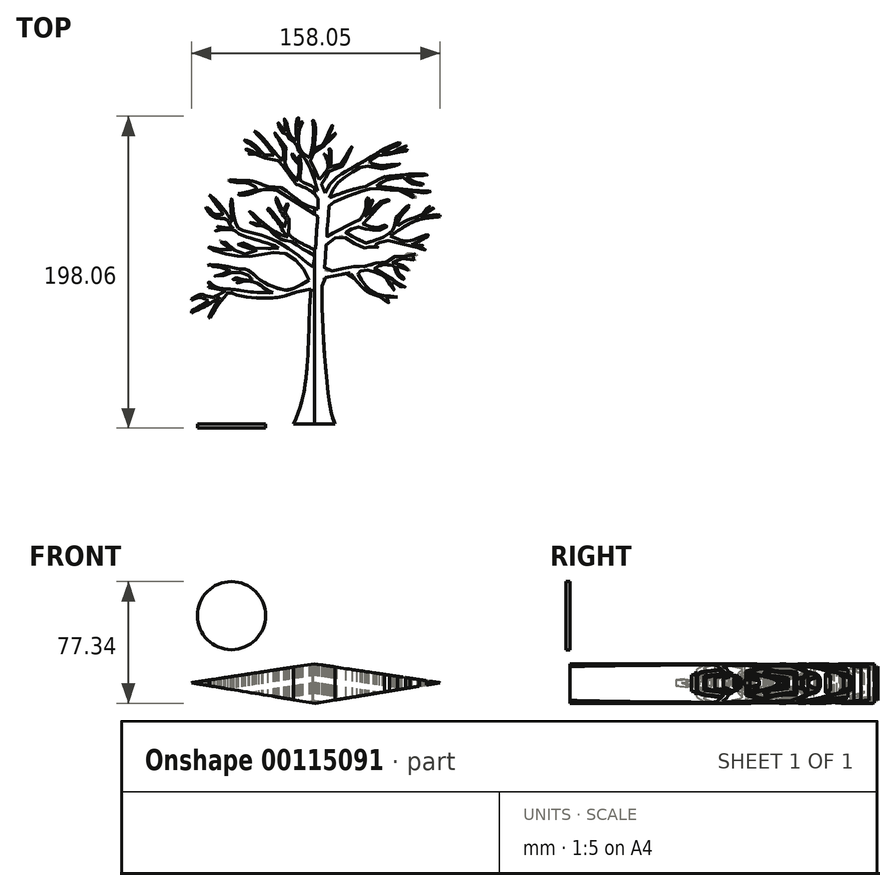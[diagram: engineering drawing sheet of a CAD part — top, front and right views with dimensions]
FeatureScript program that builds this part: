
annotation { "Feature Type Name" : "Feature", "Feature Type Description" : "" }
export const myFeature = defineFeature(function(context is Context, id is Id, definition is map)
    precondition{}
    {
        {
            var Q0;
            Q0=qCreatedBy(makeId("Top.planeOp"),FACE);
            var sketch = newSketch(context, id + "F0", { "sketchPlane" : qUnion([Q0])});
            skFitSpline(sketch, "E0", {"points": [v(-17.14, -117.95) * mm, v(-11.28, -101.28) * mm, v(-6.86, -42.52) * mm, v(-6.02, -32.17) * mm], "startDerivative": vector(3.93, 13.73) * mm, "endDerivative": vector(1.9, 26.28) * mm});
            skFitSpline(sketch, "E1", {"points": [v(-6.02, -32.17) * mm, v(-14.74, -34.04) * mm, v(-27.66, -37.49) * mm, v(-54.51, -35.53) * mm, v(-58.1, -34.04) * mm, v(-60.6, -36.76) * mm, v(-65.35, -42.8) * mm, v(-70.21, -50.73) * mm], "startDerivative": vector(-61.25, -20.1) * mm, "endDerivative": vector(-32.79, -56.2) * mm});
            skFitSpline(sketch, "E2", {"points": [v(-70.21, -50.73) * mm, v(-70.69, -50.15) * mm, v(-63.82, -37.26) * mm], "startDerivative": vector(-3.59, 1.97) * mm, "endDerivative": vector(12.9, 20.96) * mm});
            skFitSpline(sketch, "E3", {"points": [v(-63.82, -37.26) * mm, v(-74.43, -43.86) * mm, v(-80.19, -46.45) * mm, v(-82.14, -47.24) * mm, v(-82.25, -46.4) * mm, v(-79.66, -44.7) * mm, v(-71.1, -39.59) * mm], "startDerivative": vector(-42.12, -28.38) * mm, "endDerivative": vector(39.65, 25.02) * mm});
            skFitSpline(sketch, "E4", {"points": [v(-71.1, -39.59) * mm, v(-75.12, -37.8) * mm, v(-76.86, -37.53) * mm, v(-80.61, -38.69) * mm, v(-81.77, -39.11) * mm, v(-82.25, -38.9) * mm, v(-76.18, -35.63) * mm, v(-73.96, -36.05) * mm, v(-68.31, -37.53) * mm], "startDerivative": vector(-29.89, 13.9) * mm, "endDerivative": vector(37.9, -8.18) * mm});
            skFitSpline(sketch, "E5", {"points": [v(-68.31, -37.53) * mm, v(-60.65, -33.25) * mm, v(-61.34, -33.04) * mm], "startDerivative": vector(14.87, 7.27) * mm, "endDerivative": vector(-4.52, 0.44) * mm});
            skFitSpline(sketch, "E6", {"points": [v(-61.34, -33.04) * mm, v(-67.57, -31.72) * mm, v(-70.95, -31.2) * mm], "startDerivative": vector(-11.6, 2.59) * mm, "endDerivative": vector(-7.4, 1.03) * mm});
            skFitSpline(sketch, "E7", {"points": [v(-70.95, -31.2) * mm, v(-70.95, -30.66) * mm, v(-68.42, -30.77) * mm], "startDerivative": vector(-0.58, 1.97) * mm, "endDerivative": vector(4.96, -0.79) * mm});
            skFitSpline(sketch, "E8", {"points": [v(-68.42, -30.77) * mm, v(-71.4, -27.91) * mm, v(-70.6, -27.87) * mm, v(-67.1, -30.77) * mm, v(-56.96, -32.35) * mm, v(-43.07, -34.15) * mm, v(-30.3, -34.57) * mm], "startDerivative": vector(-35.84, 33.17) * mm, "endDerivative": vector(52.6, 0.18) * mm});
            skFitSpline(sketch, "E9", {"points": [v(-30.3, -34.57) * mm, v(-36.13, -31.33) * mm, v(-39.86, -28.69) * mm, v(-48.85, -27.33) * mm, v(-52.94, -28.36) * mm, v(-53.06, -28.02) * mm, v(-50.3, -27.02) * mm, v(-53.27, -26.05) * mm, v(-55.7, -26.01) * mm, v(-55.45, -25.72) * mm, v(-53.14, -25.22) * mm, v(-49.27, -26.31) * mm], "startDerivative": vector(-47.94, 23.7) * mm, "endDerivative": vector(38.86, -13.3) * mm});
            skFitSpline(sketch, "E10", {"points": [v(-49.27, -26.31) * mm, v(-46.74, -26.35) * mm, v(-42.38, -26.31) * mm, v(-47.57, -22.53) * mm, v(-51.93, -21.7) * mm, v(-55.12, -21.53) * mm, v(-60.48, -23.41) * mm, v(-66.93, -24.04) * mm, v(-67.27, -23.8) * mm, v(-66.77, -23.5) * mm, v(-61.57, -22.4) * mm, v(-57.34, -20.48) * mm, v(-58.1, -20.4) * mm, v(-59.14, -19.9) * mm, v(-62.91, -18.47) * mm, v(-68.06, -17.84) * mm, v(-71.33, -17.25) * mm, v(-72.09, -16.88) * mm, v(-72, -16.46) * mm, v(-71.12, -16.5) * mm, v(-61.74, -17.34) * mm, v(-56.29, -18.47) * mm, v(-51.89, -19.43) * mm, v(-46.57, -19.9) * mm, v(-41.83, -23.54) * mm, v(-34.08, -28.99) * mm, v(-25.83, -32.17) * mm, v(-20.38, -32.89) * mm, v(-7.18, -26.34) * mm], "startDerivative": vector(66.46, 23.55) * mm, "endDerivative": vector(214.35, 130.31) * mm});
            skFitSpline(sketch, "E11", {"points": [v(-7.18, -26.34) * mm, v(-23.22, -9.2) * mm, v(-50.68, -11.54) * mm, v(-72.4, -5.4) * mm, v(-56.58, -7.78) * mm, v(-64.95, -1) * mm, v(-58.66, -3.55) * mm, v(-55.26, -7.18) * mm, v(-47.65, -9.86) * mm, v(-40.93, -7.9) * mm, v(-46.68, -5.65) * mm, v(-52.16, -4.92) * mm, v(-53.51, -3.83) * mm, v(-50.42, -4.28) * mm, v(-48.15, -4.43) * mm, v(-49.1, -3.6) * mm, v(-49.67, -2.48) * mm, v(-46.75, -4.28) * mm, v(-42.82, -5.7) * mm, v(-38.61, -7.37) * mm, v(-36.22, -6.94) * mm, v(-26.74, -6) * mm], "startDerivative": vector(-116.92, 253.36) * mm, "endDerivative": vector(202.88, 11.26) * mm});
            skFitSpline(sketch, "E12", {"points": [v(-26.74, -6) * mm, v(-27.4, -5.29) * mm, v(-51.95, 2.9) * mm, v(-54.07, 4.7) * mm, v(-60.8, 5.62) * mm, v(-67.64, 4.5) * mm, v(-63.32, 6.09) * mm, v(-64.92, 6.89) * mm, v(-65.71, 8.02) * mm, v(-64.38, 7.49) * mm, v(-55.34, 6.35) * mm], "startDerivative": vector(-3.14, 13.4) * mm, "endDerivative": vector(77.7, -4.3) * mm});
            skFitSpline(sketch, "E13", {"points": [v(-55.34, 6.35) * mm, v(-56.87, 7.68) * mm, v(-59.8, 12.08) * mm, v(-67.84, 13.74) * mm, v(-72.7, 20) * mm, v(-69.57, 17.53) * mm, v(-67.64, 15.47) * mm, v(-61.52, 15.33) * mm, v(-61.99, 16.13) * mm, v(-70.7, 27.64) * mm], "startDerivative": vector(-22.53, 12.79) * mm, "endDerivative": vector(-57, 78.87) * mm});
            skFitSpline(sketch, "E14", {"points": [v(-70.7, 27.64) * mm, v(-64.72, 22.45) * mm, v(-55.87, 10.21) * mm], "startDerivative": vector(14.04, -10.51) * mm, "endDerivative": vector(15.55, -23.64) * mm});
            skFitSpline(sketch, "E15", {"points": [v(-55.87, 10.21) * mm, v(-57.13, 22.92) * mm, v(-56.47, 25.31) * mm, v(-55.87, 21.12) * mm, v(-54.07, 10.21) * mm, v(-51.75, 5.82) * mm, v(-46.56, 4.36) * mm, v(-29, -1.5) * mm, v(-4.85, -18.32) * mm], "startDerivative": vector(-16.04, 99.74) * mm, "endDerivative": vector(109.24, -87.43) * mm});
            skFitSpline(sketch, "E16", {"points": [v(-4.85, -18.32) * mm, v(-3.65, -11.34) * mm, v(-3.92, -10.8) * mm, v(-13.16, -5.49) * mm, v(-18.62, -1.96) * mm, v(-26.2, 0) * mm, v(-35.07, 7.69) * mm, v(-38.26, 7.49) * mm, v(-45.3, 10.68) * mm, v(-44.51, 10.88) * mm, v(-43.51, 10.28) * mm, v(-39.06, 8.35) * mm, v(-36.93, 8.69) * mm, v(-37.93, 9.48) * mm, v(-45.3, 17.17) * mm, v(-45.5, 17.97) * mm, v(-44.44, 17.17) * mm, v(-40.63, 13.31) * mm, v(-31.61, 6.16) * mm, v(-20.61, 0.7) * mm], "startDerivative": vector(23.47, 124.9) * mm, "endDerivative": vector(98.14, 5.97) * mm});
            skFitSpline(sketch, "E17", {"points": [v(-20.61, 0.7) * mm, v(-24.2, 5.42) * mm, v(-26, 8.55) * mm, v(-33.59, 18.93) * mm, v(-33.59, 19.33) * mm, v(-32.99, 19.26) * mm, v(-23.14, 6.89) * mm], "startDerivative": vector(-23.28, 28.66) * mm, "endDerivative": vector(41.77, -57.86) * mm});
            skFitSpline(sketch, "E18", {"points": [v(-23.14, 6.89) * mm, v(-21.61, 11.68) * mm], "startDerivative": vector(1.53, 4.79) * mm, "endDerivative": vector(1.53, 4.79) * mm});
            skFitSpline(sketch, "E19", {"points": [v(-21.61, 11.68) * mm, v(-25, 16.86) * mm, v(-28.4, 25.84) * mm, v(-27.8, 25.84) * mm, v(-27.27, 24.65) * mm, v(-23.54, 17.86) * mm, v(-22.63, 19.86) * mm, v(-21.61, 20.79) * mm, v(-20.81, 22.05) * mm, v(-20.22, 21.52) * mm, v(-20.81, 20.66) * mm, v(-22.42, 16.53) * mm], "startDerivative": vector(-22.32, 29) * mm, "endDerivative": vector(-12.72, -43.1) * mm});
            skFitSpline(sketch, "E20", {"points": [v(-22.42, 16.53) * mm, v(-20.31, 12.68) * mm, v(-19.93, 10.55) * mm, v(-20.31, 3.05) * mm], "startDerivative": vector(7.63, -12.78) * mm, "endDerivative": vector(-1.42, -20.17) * mm});
            skFitSpline(sketch, "E21", {"points": [v(-20.31, 3.05) * mm, v(-16.12, -0.8) * mm, v(-3.6, -7.13) * mm, v(-3.26, -6.96) * mm, v(-2.25, 7.83) * mm, v(-2.12, 14.29) * mm], "startDerivative": vector(15.8, -20) * mm, "endDerivative": vector(-12.14, 4.1) * mm});
            skFitSpline(sketch, "E22", {"points": [v(-52.28, 28.5) * mm, v(-48.13, 28.97) * mm, v(-40.94, 31.23) * mm, v(-39.2, 32.07) * mm, v(-39.65, 32.56) * mm, v(-40.85, 32.6) * mm, v(-45.69, 34.83) * mm, v(-54.03, 35.45) * mm, v(-59, 36.87) * mm, v(-59, 37.4) * mm, v(-56.52, 37.05) * mm, v(-45.24, 36.6) * mm, v(-37.07, 34.2) * mm, v(-31.48, 32.78) * mm, v(-26.33, 32.52) * mm, v(-21.27, 29.94) * mm, v(-11.5, 22.48) * mm, v(-1.65, 18.49) * mm], "startDerivative": vector(66.06, 8.87) * mm, "endDerivative": vector(114.77, -35.11) * mm});
            skLineSegment(sketch, "E23", {"start": v(-27.3, 30.4) * mm, "end": v(-2.12, 14.29) * mm});
            skFitSpline(sketch, "E24", {"points": [v(-1.65, 18.49) * mm, v(-1.45, 24.39) * mm, v(-1.47, 24.8) * mm, v(-1.82, 25.43) * mm, v(-5.7, 29.72) * mm, v(-14.62, 34.02) * mm, v(-15.6, 34.58) * mm, v(-26.86, 49.48) * mm, v(-27.16, 49.55) * mm], "startDerivative": vector(1.62, 48.58) * mm, "endDerivative": vector(-5.15, -2.9) * mm});
            skFitSpline(sketch, "E25", {"points": [v(-27.16, 49.55) * mm, v(-35.09, 50.95) * mm, v(-35.73, 51.15) * mm, v(-36.52, 51.58) * mm, v(-37.54, 51.94) * mm, v(-40.76, 53.37) * mm, v(-41.14, 53.43) * mm, v(-46.15, 53.65) * mm, v(-43.56, 54.09) * mm, v(-47.97, 56.7) * mm, v(-44.87, 56.11) * mm, v(-42.36, 54.6) * mm, v(-40.3, 54.03) * mm, v(-37.47, 52.89) * mm], "startDerivative": vector(-75.54, 13.06) * mm, "endDerivative": vector(34.7, -16.07) * mm});
            skFitSpline(sketch, "E26", {"points": [v(-37.47, 52.89) * mm, v(-38.58, 54.3) * mm, v(-43.27, 58.75) * mm, v(-48.28, 62.44) * mm, v(-46.15, 62.04) * mm, v(-38.77, 56.35) * mm, v(-35.76, 53.08) * mm, v(-32.15, 52.89) * mm, v(-29.37, 52.65) * mm], "startDerivative": vector(-11.68, 15.44) * mm, "endDerivative": vector(25.9, -3.8) * mm});
            skFitSpline(sketch, "E27", {"points": [v(-29.37, 52.65) * mm, v(-34.96, 60.06) * mm, v(-42.23, 68.23) * mm], "startDerivative": vector(-11.1, 15.38) * mm, "endDerivative": vector(-14.57, 15.77) * mm});
            skFitSpline(sketch, "E28", {"points": [v(-42.23, 68.23) * mm, v(-41.28, 68.23) * mm, v(-23.87, 48.52) * mm, v(-23.83, 48.48) * mm, v(-23.61, 57.44) * mm, v(-24.36, 58.75) * mm, v(-27.67, 64.62) * mm, v(-29.03, 66.72) * mm, v(-29.13, 67.02) * mm, v(-22.16, 58.1) * mm, v(-22, 57.64) * mm, v(-22.6, 46.71) * mm, v(-22.5, 46.36) * mm, v(-16.09, 38.18) * mm, v(-14.08, 36.58) * mm], "startDerivative": vector(16.33, 15.47) * mm, "endDerivative": vector(27.04, -14.44) * mm});
            skFitSpline(sketch, "E29", {"points": [v(-27.3, 30.4) * mm, v(-36.46, 30.94) * mm, v(-44.8, 28.26) * mm, v(-51.7, 27.62) * mm, v(-52.28, 28.5) * mm], "startDerivative": vector(-30.11, 4.82) * mm, "endDerivative": vector(-2.56, 9.45) * mm});
            skFitSpline(sketch, "E30", {"points": [v(-14.08, 36.58) * mm, v(-14.08, 40.86) * mm, v(-13.72, 42.16) * mm, v(-13.38, 46) * mm, v(-13.17, 46.35) * mm, v(-13.87, 47.23) * mm, v(-17.94, 52.2) * mm, v(-17.5, 54.38) * mm, v(-17.33, 54.38) * mm, v(-17.18, 52.9) * mm, v(-13.47, 48.07) * mm, v(-13.13, 47.99) * mm, v(-13.97, 51.83) * mm, v(-14.14, 53.21) * mm, v(-13.4, 52.17) * mm, v(-12.13, 45.8) * mm, v(-12.28, 45.5) * mm, v(-12.84, 40.36) * mm, v(-12.7, 36.1) * mm, v(-12.56, 35.96) * mm, v(-10.52, 35.13) * mm, v(-5.24, 32.9) * mm, v(-1.89, 30.28) * mm], "startDerivative": vector(-4.06, 81.98) * mm, "endDerivative": vector(47.57, -44.67) * mm});
            skFitSpline(sketch, "E31", {"points": [v(-1.89, 30.28) * mm, v(-4.65, 39.4) * mm, v(-8.63, 48.68) * mm, v(-10.13, 51.04) * mm, v(-14.63, 56.78) * mm, v(-15.3, 59.78) * mm, v(-20.1, 63.44) * mm, v(-21.47, 66.3) * mm, v(-23.5, 66.84) * mm, v(-26.9, 72.73) * mm, v(-26.6, 73.85) * mm, v(-25.53, 71.96) * mm, v(-22.8, 67.9) * mm, v(-21.63, 67.53) * mm, v(-21.71, 68.52) * mm, v(-22.81, 76.02) * mm, v(-22.29, 76.23) * mm, v(-21.77, 75) * mm, v(-19.33, 65.4) * mm, v(-15.26, 62.42) * mm], "startDerivative": vector(-28.5, 105.1) * mm, "endDerivative": vector(75.49, -28.96) * mm});
            skFitSpline(sketch, "E32", {"points": [v(-15.26, 62.42) * mm, v(-14.8, 76.02) * mm, v(-13.84, 77.57) * mm, v(-13.96, 76.02) * mm, v(-13.84, 70.71) * mm, v(-11.7, 74.6) * mm, v(-11.33, 74.77) * mm, v(-13.66, 68.03) * mm, v(-13.78, 66.48) * mm, v(-13.48, 58.01) * mm, v(-7.04, 51.1) * mm], "startDerivative": vector(-3.61, 94.5) * mm, "endDerivative": vector(56.5, -39.34) * mm});
            skFitSpline(sketch, "E33", {"points": [v(-7.04, 51.1) * mm, v(-4.83, 60.75) * mm, v(-5, 74.95) * mm, v(-5.19, 75.3) * mm, v(-4.06, 74.23) * mm, v(-4.06, 57.35) * mm], "startDerivative": vector(10.87, 32.93) * mm, "endDerivative": vector(-6.74, -67.77) * mm});
            skFitSpline(sketch, "E34", {"points": [v(-4.06, 57.35) * mm, v(1.79, 60.22) * mm, v(6.92, 71.13) * mm, v(7.81, 71.73) * mm, v(4.24, 62.54) * mm, v(4.47, 62.36) * mm, v(9.66, 66.72) * mm, v(10.02, 66.48) * mm, v(9.07, 65.59) * mm, v(4.3, 60.75) * mm, v(3.7, 60.52) * mm, v(2.62, 58.9) * mm, v(-4.77, 53.78) * mm, v(-4.9, 53.06) * mm, v(-6.5, 49.3) * mm], "startDerivative": vector(63.62, 11.93) * mm, "endDerivative": vector(-30.11, -58.53) * mm});
            skFitSpline(sketch, "E35", {"points": [v(-6.5, 49.3) * mm, v(-3.13, 42.64) * mm, v(-0.87, 37.38) * mm], "startDerivative": vector(6.73, -12.83) * mm, "endDerivative": vector(4.48, -10.98) * mm});
            skFitSpline(sketch, "E36", {"points": [v(-0.87, 37.38) * mm, v(3.94, 43.16) * mm, v(4.76, 47.22) * mm, v(2.43, 53) * mm, v(1.98, 53.3) * mm, v(2.36, 53.53) * mm, v(5.37, 49.55) * mm], "startDerivative": vector(22.46, 24.31) * mm, "endDerivative": vector(16.88, -28.84) * mm});
            skFitSpline(sketch, "E37", {"points": [v(5.37, 49.55) * mm, v(5.58, 54.8) * mm, v(5.7, 56.93) * mm, v(6.7, 55.86) * mm], "startDerivative": vector(0.83, 11.66) * mm, "endDerivative": vector(5.05, -6.97) * mm});
            skFitSpline(sketch, "E38", {"points": [v(6.7, 55.86) * mm, v(6.7, 48.85) * mm, v(6.09, 45.33) * mm], "startDerivative": vector(0.43, -13.05) * mm, "endDerivative": vector(-1.8, -7.7) * mm});
            skFitSpline(sketch, "E39", {"points": [v(6.09, 45.33) * mm, v(11.44, 46.77) * mm, v(12.99, 47.61) * mm, v(19.32, 58) * mm, v(19.68, 58.42) * mm, v(19.88, 58.3) * mm, v(13.94, 45.78) * mm, v(13.55, 45.59) * mm, v(5.64, 42.46) * mm, v(5.33, 42.12) * mm, v(0.56, 34.5) * mm], "startDerivative": vector(52.36, 15.08) * mm, "endDerivative": vector(-42.77, -66.51) * mm});
            skFitSpline(sketch, "E40", {"points": [v(0.56, 34.5) * mm, v(2.1, 30.73) * mm, v(2.82, 28.92) * mm], "startDerivative": vector(2.86, -6.96) * mm, "endDerivative": vector(1.58, -4.02) * mm});
            skFitSpline(sketch, "E41", {"points": [v(2.82, 28.92) * mm, v(6.1, 34.4) * mm, v(13.66, 41.04) * mm, v(27.68, 49) * mm, v(44.34, 58.76) * mm, v(51.36, 61.04) * mm, v(51.2, 60.67) * mm, v(39.14, 54.4) * mm], "startDerivative": vector(23.38, 45.86) * mm, "endDerivative": vector(-94.21, -45.05) * mm});
            skFitSpline(sketch, "E42", {"points": [v(39.14, 54.4) * mm, v(39.35, 54) * mm, v(46.92, 54.8) * mm, v(48.4, 55.94) * mm, v(54.97, 59.34) * mm, v(55.34, 59.26) * mm, v(49.8, 55.7) * mm, v(49.92, 55.41) * mm, v(53.27, 55.94) * mm, v(55.5, 55.84) * mm, v(55.5, 55.6) * mm, v(53.22, 55.52) * mm, v(49.98, 54.7) * mm, v(47.74, 54.4) * mm, v(45.06, 53.45) * mm, v(36.7, 52.7) * mm, v(35.76, 52.17) * mm, v(29.12, 47.95) * mm, v(29.68, 47.79) * mm, v(39.99, 46.03) * mm, v(40.89, 46.2) * mm, v(51.04, 47.12) * mm, v(51.12, 46.6) * mm, v(49.76, 46.35) * mm, v(39.56, 44.28) * mm, v(38.4, 44.33) * mm, v(27.34, 46) * mm, v(25.03, 44.97) * mm, v(11.66, 35.96) * mm, v(5.63, 25.84) * mm], "startDerivative": vector(-2.17, -37.4) * mm, "endDerivative": vector(-62.18, -165.42) * mm});
            skFitSpline(sketch, "E43", {"points": [v(5.63, 25.84) * mm, v(22.2, 31.53) * mm, v(29.2, 33.22) * mm, v(30.85, 34.16) * mm, v(40.32, 38.97) * mm, v(41.67, 39.31) * mm, v(62.07, 40.93) * mm, v(67.7, 40.14) * mm, v(67.63, 39.87) * mm, v(66.73, 39.91) * mm, v(54.56, 39.39) * mm], "startDerivative": vector(103.06, 38.8) * mm, "endDerivative": vector(-108.97, -7.39) * mm});
            skFitSpline(sketch, "E44", {"points": [v(54.56, 39.39) * mm, v(58.95, 36.23) * mm, v(65.57, 34.39) * mm, v(65.72, 34.05) * mm, v(58.61, 34.73) * mm, v(52.3, 38.79) * mm, v(51.59, 38.67) * mm, v(43.13, 37.43) * mm, v(35.7, 33.19) * mm], "startDerivative": vector(26.64, -26.8) * mm, "endDerivative": vector(-38.96, -30.57) * mm});
            skFitSpline(sketch, "E45", {"points": [v(35.7, 33.19) * mm, v(67.26, 30) * mm, v(69.81, 30) * mm, v(70, 29.77) * mm, v(66.24, 28.87) * mm, v(65.38, 28.9) * mm, v(54.78, 30.03) * mm], "startDerivative": vector(98.8, -11.95) * mm, "endDerivative": vector(-59.94, 6) * mm});
            skFitSpline(sketch, "E46", {"points": [v(54.78, 30.03) * mm, v(59, 27.17) * mm, v(60.76, 26.39) * mm, v(61.13, 26.12) * mm, v(60.8, 25.82) * mm, v(57.64, 26.54) * mm, v(51.74, 30.03) * mm, v(50.87, 30.33) * mm, v(38.59, 31.35) * mm, v(30.5, 31.2) * mm, v(5.63, 21.76) * mm, v(5.4, 21.43) * mm, v(5.07, 15.75) * mm, v(4.12, 1.12) * mm, v(4.44, 1.3) * mm, v(25.11, 12.08) * mm], "startDerivative": vector(68.6, -50.32) * mm, "endDerivative": vector(202.56, 100.6) * mm});
            skFitSpline(sketch, "E47", {"points": [v(25.11, 12.08) * mm, v(28.7, 18.88) * mm, v(29.12, 24.04) * mm, v(30.18, 25.91) * mm, v(30.47, 25.74) * mm, v(30.33, 24.1) * mm, v(30.25, 19.57) * mm], "startDerivative": vector(20.72, 25.34) * mm, "endDerivative": vector(0.63, -24.43) * mm});
            skFitSpline(sketch, "E48", {"points": [v(30.25, 19.57) * mm, v(32.45, 24.03) * mm, v(33.2, 24.28) * mm, v(33.2, 23.64) * mm, v(28.13, 13.9) * mm], "startDerivative": vector(7.01, 18.49) * mm, "endDerivative": vector(-15.03, -27.06) * mm});
            skFitSpline(sketch, "E49", {"points": [v(28.13, 13.9) * mm, v(30.5, 16.1) * mm, v(38.62, 23.79) * mm, v(39.69, 24) * mm, v(45, 24.89) * mm, v(45.22, 24.74) * mm, v(44.9, 24.1) * mm, v(44.37, 24.1) * mm, v(39.33, 22.47) * mm, v(38.52, 21.9) * mm, v(31.57, 14.25) * mm, v(30.96, 13.9) * mm, v(30.6, 13) * mm, v(26.67, 9.88) * mm, v(26.57, 9.53) * mm, v(36.53, 6.94) * mm, v(43.2, 9.32) * mm, v(43.3, 8.71) * mm, v(36.18, 5.1) * mm, v(23.37, 7.47) * mm, v(23.1, 7.47) * mm, v(16.03, 4.1) * mm, v(16.03, 3.64) * mm, v(28.87, -3.03) * mm], "startDerivative": vector(41, 35.7) * mm, "endDerivative": vector(198.23, -96.55) * mm});
            skFitSpline(sketch, "E50", {"points": [v(28.87, -3.03) * mm, v(37.68, 0) * mm, v(46.17, 5.86) * mm, v(47.87, 12.97) * mm, v(49.35, 14.58) * mm, v(55.78, 20.74) * mm, v(56.5, 20.56) * mm, v(55.92, 19.45) * mm, v(50.1, 12.56) * mm, v(49.35, 7.87) * mm], "startDerivative": vector(57.53, 18.18) * mm, "endDerivative": vector(2.55, -41.47) * mm});
            skFitSpline(sketch, "E51", {"points": [v(49.35, 7.87) * mm, v(55.6, 11.76) * mm, v(64.99, 15.74) * mm, v(68.74, 20.3) * mm, v(69.54, 20.03) * mm, v(68.83, 19.5) * mm, v(67.85, 17.75) * mm, v(70.57, 18.64) * mm, v(72.1, 19.76) * mm, v(72.58, 19.62) * mm, v(71.87, 18.78) * mm, v(63.74, 13.86) * mm, v(68.43, 14.49) * mm, v(76.34, 14.66) * mm, v(76.78, 14.13) * mm, v(71.33, 13.32) * mm, v(59.98, 10.96) * mm, v(44.34, 1.4) * mm], "startDerivative": vector(72.42, 56.3) * mm, "endDerivative": vector(-132.53, -93.7) * mm});
            skFitSpline(sketch, "E52", {"points": [v(44.34, 1.4) * mm, v(48.9, -0.35) * mm, v(55.74, -1.69) * mm, v(67.4, 2.15) * mm, v(69, 2.06) * mm, v(68.96, 1.93) * mm, v(58.55, -3.83) * mm, v(57.7, -3.9) * mm], "startDerivative": vector(29.01, -10.63) * mm, "endDerivative": vector(-6.45, -1.07) * mm});
            skFitSpline(sketch, "E53", {"points": [v(57.7, -3.9) * mm, v(60.26, -4.47) * mm, v(64.29, -3.9) * mm, v(64.97, -3.9) * mm, v(64.77, -4.55) * mm, v(62.76, -5.05) * mm, v(62.74, -5.18) * mm, v(66.27, -6.7) * mm, v(67.03, -6.83) * mm, v(67.23, -7.23) * mm, v(66.5, -7.32) * mm, v(61.2, -5.77) * mm, v(57.97, -5.07) * mm, v(43.87, -1.7) * mm, v(43.04, -1.5) * mm, v(39.24, -2.2) * mm, v(33.99, -4.83) * mm, v(36.73, -4.95) * mm, v(37.02, -5.5) * mm, v(32.56, -5.55) * mm, v(28.08, -6.08) * mm], "startDerivative": vector(43.65, -8.8) * mm, "endDerivative": vector(-58.2, -19.6) * mm});
            skFitSpline(sketch, "E54", {"points": [v(28.08, -6.08) * mm, v(26.83, -6.08) * mm, v(14.13, 1.43) * mm, v(11.74, 1.8) * mm, v(4.05, -3.44) * mm, v(3.21, -6.08) * mm, v(2.5, -18.12) * mm, v(2.14, -20.14) * mm, v(3.21, -21.1) * mm, v(19.44, -18.24) * mm, v(30.9, -17.28) * mm, v(38.76, -14.54) * mm, v(43.42, -15.25) * mm, v(43.63, -14.86) * mm, v(47.6, -11.2) * mm, v(48.45, -11.07) * mm, v(53.14, -11.78) * mm, v(53.46, -11.78) * mm, v(55.42, -9.64) * mm, v(56.1, -9.6) * mm, v(61.32, -10.08) * mm, v(62.84, -10.98) * mm, v(62.21, -11.02) * mm, v(56.45, -10.8) * mm, v(55.96, -11.42) * mm, v(55.82, -12.1) * mm, v(56.23, -12.14) * mm, v(61.63, -13.26) * mm, v(62.44, -13.97) * mm, v(62, -14.02) * mm, v(53, -12.99) * mm, v(48.72, -12.8) * mm, v(45.73, -15.58) * mm, v(46.04, -15.71) * mm, v(54.66, -18.13) * mm, v(56.9, -20.4) * mm, v(56.45, -20.63) * mm, v(55.56, -20.14) * mm, v(48.72, -17.63) * mm], "startDerivative": vector(-50.57, -22.15) * mm, "endDerivative": vector(-218.02, 70.48) * mm});
            skFitSpline(sketch, "E55", {"points": [v(48.72, -17.63) * mm, v(48.4, -17.85) * mm, v(49.72, -21.81) * mm, v(53.06, -25.22) * mm, v(53.34, -25.81) * mm, v(52.92, -26.01) * mm, v(48.96, -23.37) * mm, v(46.65, -17.63) * mm, v(46.14, -17.47) * mm, v(40.62, -16.7) * mm, v(34.23, -19.25) * mm], "startDerivative": vector(-10.24, -2.41) * mm, "endDerivative": vector(-38.2, -23.3) * mm});
            skFitSpline(sketch, "E56", {"points": [v(34.23, -19.25) * mm, v(45.86, -26.13) * mm, v(48.17, -27.8) * mm, v(52.52, -30.43) * mm, v(53.84, -30.85) * mm, v(54.03, -31.28) * mm, v(51.28, -31.14) * mm, v(44.75, -27.16) * mm, v(46.36, -31.56) * mm, v(47.07, -32.46) * mm, v(46.98, -33.03) * mm, v(44.75, -30.62) * mm, v(42.05, -25.4) * mm, v(30.22, -20.06) * mm, v(28.9, -20.2) * mm, v(22.83, -21.38) * mm, v(23.6, -22.38) * mm, v(28.13, -29.72) * mm, v(36.85, -35.63) * mm, v(43.05, -36.53) * mm, v(48.8, -37.22) * mm], "startDerivative": vector(160.83, -92.7) * mm, "endDerivative": vector(104.95, -16.8) * mm});
            skFitSpline(sketch, "E57", {"points": [v(48.8, -37.22) * mm, v(48.8, -37.55) * mm, v(40.6, -37.47) * mm, v(40.83, -37.9) * mm, v(43.72, -40.38) * mm, v(43.49, -41.04) * mm, v(42.61, -40.43) * mm, v(38.37, -37.22) * mm, v(37.97, -37.03) * mm, v(30.66, -34.52) * mm, v(19.44, -22.52) * mm, v(18.55, -22.01) * mm, v(6.26, -24.4) * mm, v(1.57, -25.35) * mm, v(1.2, -25.82) * mm, v(2.16, -67.97) * mm, v(9.3, -117.95) * mm], "startDerivative": vector(14.78, -23.78) * mm, "endDerivative": vector(49.5, -50.3) * mm});
            skLineSegment(sketch, "E58", {"start": v(0, 0) * mm, "end": v(0, -89.11) * mm, "construction": true});
            skLineSegment(sketch, "E59", {"start": v(-17.14, -117.95) * mm, "end": v(9.3, -117.95) * mm});
            skSolve(sketch);
        }
        {
            var Q0;
            Q0=qSketchRegion(id+"F0",true);
            extrude(context, id + "F1", {"entities" : qUnion([Q0]), "depth" : 25.4 * mm});
        }
        {
            var Q0;
            Q0=makeQuery(id+"F1.opExtrude","SWEPT_FACE",FACE,{"disambiguationData":[OSD([sQuery(id+"F0.wireOp",EDGE,"E59")])]});
            var sketch = newSketch(context, id + "F2", { "sketchPlane" : qUnion([Q0])});
            skLineSegment(sketch, "E60.bottom", {"start": v(82.38, 32.3) * mm, "end": v(-97.8, 32.3) * mm});
            skLineSegment(sketch, "E60.top", {"start": v(82.38, -17) * mm, "end": v(-97.8, -17) * mm});
            skLineSegment(sketch, "E60.left", {"start": v(82.38, 32.3) * mm, "end": v(82.38, -17) * mm});
            skLineSegment(sketch, "E60.right", {"start": v(-97.8, 32.3) * mm, "end": v(-97.8, -17) * mm});
            skLineSegment(sketch, "E61", {"start": v(-3.92, 25.4) * mm, "end": v(-82, 13.42) * mm});
            skLineSegment(sketch, "E62", {"start": v(-82, 13.42) * mm, "end": v(-3.5, 0.37) * mm});
            skLineSegment(sketch, "E63", {"start": v(-3.5, 0.37) * mm, "end": v(76.04, 13.42) * mm});
            skLineSegment(sketch, "E64", {"start": v(76.04, 13.42) * mm, "end": v(-3.92, 25.4) * mm});
            skSolve(sketch);
        }
        {
            var Q0;
            Q0=makeQuery(id+"F2.imprint","IMPRINT",FACE,{"disambiguationData":[TD([[makeQuery(id+"F2.imprint","IMPRINT",EDGE,{"derivedFrom":sQuery(id+"F2.wireOp",EDGE,"E60.bottom")}),1.0]])]});
            var Q1;
            {var subQ0=sQuery(id+"F2.wireOp",EDGE,"E61");var subQ1=sQuery(id+"F0.wireOp",EDGE,"E59");var subQ2=makeQuery(id+"F1.opExtrude","CAP_EDGE",EDGE,{"disambiguationData":[OSD([subQ1])],"isStart":false});var subQ3=makeQuery(id+"F2.imprint","INTERSECT",VERTEX,{"derivedFrom":[subQ2,sQuery(id+"F2.wireOp",EDGE,"APYxddTp-fbFp-GE4o-hfZb-D1Turj3EziGu"),subQ0]});Q1=makeQuery(id+"F2.imprint","IMPRINT",FACE,{"disambiguationData":[TD([[makeQuery(id+"F2.imprint","IMPRINT",EDGE,{"disambiguationData":[TD([[subQ3,-1.0]])],"derivedFrom":subQ0}),-1.0]])]});}
            var Q2;
            {var subQ0=sQuery(id+"F2.wireOp",EDGE,"APYxddTp-fbFp-GE4o-hfZb-D1Turj3EziGu");var subQ1=sQuery(id+"F0.wireOp",EDGE,"E59");var subQ2=makeQuery(id+"F1.opExtrude","CAP_EDGE",EDGE,{"disambiguationData":[OSD([subQ1])],"isStart":false});var subQ3=makeQuery(id+"F2.imprint","INTERSECT",VERTEX,{"derivedFrom":[subQ2,subQ0,sQuery(id+"F2.wireOp",EDGE,"E61")]});Q2=makeQuery(id+"F2.imprint","IMPRINT",FACE,{"disambiguationData":[TD([[makeQuery(id+"F2.imprint","IMPRINT",EDGE,{"disambiguationData":[TD([[subQ3,1.0]])],"derivedFrom":subQ0}),-1.0]])]});}
            var Q3;
            {var subQ0=sQuery(id+"F2.wireOp",EDGE,"E63");var subQ1=sQuery(id+"F0.wireOp",EDGE,"E59");var subQ2=makeQuery(id+"F1.opExtrude","CAP_EDGE",EDGE,{"disambiguationData":[OSD([subQ1])],"isStart":true});var subQ3=makeQuery(id+"F2.imprint","INTERSECT",VERTEX,{"derivedFrom":[subQ2,sQuery(id+"F2.wireOp",EDGE,"E62"),subQ0]});Q3=makeQuery(id+"F2.imprint","IMPRINT",FACE,{"disambiguationData":[TD([[makeQuery(id+"F2.imprint","IMPRINT",EDGE,{"disambiguationData":[TD([[subQ3,-1.0]])],"derivedFrom":subQ0}),-1.0]])]});}
            var Q4;
            {var subQ0=sQuery(id+"F2.wireOp",EDGE,"E62");var subQ1=sQuery(id+"F0.wireOp",EDGE,"E59");var subQ2=makeQuery(id+"F1.opExtrude","CAP_EDGE",EDGE,{"disambiguationData":[OSD([subQ1])],"isStart":true});var subQ3=makeQuery(id+"F2.imprint","INTERSECT",VERTEX,{"derivedFrom":[subQ2,subQ0,sQuery(id+"F2.wireOp",EDGE,"E63")]});Q4=makeQuery(id+"F2.imprint","IMPRINT",FACE,{"disambiguationData":[TD([[makeQuery(id+"F2.imprint","IMPRINT",EDGE,{"disambiguationData":[TD([[subQ3,1.0]])],"derivedFrom":subQ0}),-1.0]])]});}
            var Q5;
            {var subQ0=sQuery(id+"F2.wireOp",EDGE,"E64");var subQ1=sQuery(id+"F0.wireOp",EDGE,"E59");var subQ2=makeQuery(id+"F1.opExtrude","CAP_EDGE",EDGE,{"disambiguationData":[OSD([subQ1])],"isStart":false});var subQ3=makeQuery(id+"F2.imprint","INTERSECT",VERTEX,{"derivedFrom":[subQ2,sQuery(id+"F2.wireOp",EDGE,"E61"),subQ0]});Q5=makeQuery(id+"F2.imprint","IMPRINT",FACE,{"disambiguationData":[TD([[makeQuery(id+"F2.imprint","IMPRINT",EDGE,{"disambiguationData":[TD([[subQ3,1.0]])],"derivedFrom":subQ0}),-1.0]])]});}
            extrude(context, id + "F3", {"entities" : qUnion([Q0, Q1, Q2, Q3, Q4, Q5]), "operationType" : NewBodyOperationType.REMOVE, "endBound" : BoundingType.THROUGH_ALL, "oppositeDirection" : true, "depth" : 25.4 * mm});
        }
        {
            var Q0;
            Q0=makeQuery(id+"F1.opExtrude","SWEPT_FACE",FACE,{"disambiguationData":[OSD([sQuery(id+"F0.wireOp",EDGE,"E59")])]});
            var sketch = newSketch(context, id + "F4", { "sketchPlane" : qUnion([Q0])});
            skCircle(sketch, "E65", {"center": v(-56.54, 56.07) * mm, "radius": 21.64 * mm});
            skSolve(sketch);
        }
        {
            var Q0;
            Q0=makeQuery(id+"F4.imprint","IMPRINT",FACE,{"disambiguationData":[TD([[makeQuery(id+"F4.imprint","IMPRINT",EDGE,{"derivedFrom":sQuery(id+"F4.wireOp",EDGE,"E65")}),1.0]])]});
            extrude(context, id + "F5", {"entities" : qUnion([Q0]), "depth" : 2.54 * mm});
        }
    });
